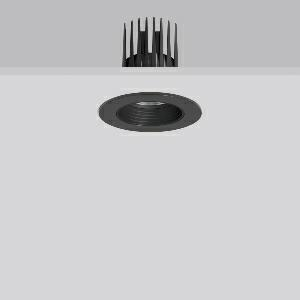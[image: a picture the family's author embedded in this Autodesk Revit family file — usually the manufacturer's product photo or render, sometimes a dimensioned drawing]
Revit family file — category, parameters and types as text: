
# Revit family: heledon_mini_e_901743_003_32de
name_source: partatom
category: Lighting Fixtures
units: mm (PartAtom-declared; Revit-internal decimal feet)

## family parameters
Cut with Voids When Loaded = No
Host = Face
Light Source = No
Part Type = Normal
Room Calculation Point = No
Round Connector Dimension = Use Diameter
Shared = No

## types (1)
- HELEDON mini E (1 x LED Modul 930, 2250 lm, 3000)
    Apparent Load = 20 VA
    Approval mark = CE
    CIE Flux Codes = 99 100 100 100 100
    Color Rendering = 90
    Color Temperature = 3000
    Default Elevation = 1800 mm
    Description = Series: HELEDON mini
Round recessed downlight. Housing: die-cast aluminium, powder-coated. Black plastic ring and recessed LED to prevent glare from the side. Optical assembly with lens made of plastic (polycarbonate) for the best homogeneous light distribution - can be changed without tools. Best colour rendering index Ra>90. Suitable for Recessed ceiling mounting. Installation without tools thanks to spring fastening system. Including separate LED converter with connecting cable 600 mm.High quality converter without flickering and stroboscopic effect. Through-wiring box (5 pole) available as accessory. The following accessories can be mounted without use of tools: interchangeable lenses, decorative glasses, honeycomb louvre, clear and frosted diffusers, white interchangeable plastic ring. 
Colour: deep black, matt (RAL 9005)
Diameter: 124 mm
Height: 3 mm
Cut-out diameter: 114 mm
Recess height: 170 mm
Luminaire: recess height: 120 mm
Lamp: LED
Socket: without socket
Colour temperature: 3000K
Colour rendering index (CRI): 92
System power: 20 W
Rated luminous flux: 2250 lm
Luminous efficiency: 113 lm/W
Control gear: Regulated power supply
Protection class: II
Type of protection: IP 20
    Height = 0 mm  [stored 0 ft]
    Lamp = 1 x LED Modul 930
    Lamp Light Flux = 2250 lm
    Lamp count = 1
    Length = 124 mm  [stored 0.406824 ft]
    Lifetime = 50000 h
    Luminous efficacy = 113 lm/W
    Manufacturer = RZB
    ModVariant = No
    Model = 901743.003
    Mounting Place = Ceiling
    Mounting Type = Recessed
    Number of Poles = 1
    OnlyDefault = Yes
    Power Factor = 1
    Product Name = HELEDON mini E
    Product group = Recessed downlights
    ProductGroupID = 402
    Protection Class = Protection class II
    Protection Degree = IP 20
    RLX_Detail_Level = 1
    RLX_Emergency_Light_Flux = 0 lm
    RLX_Emergency_Type = 0
    RLX_Emergency_Type_DB = No
    RlxData = <blob elided: 122801 chars, md5=823b8166>
    Socket = socket
    Standby Power = 0 W
    System Light Flux = 2250 lm
    System Power = 20 W
    Type Comments = Product without accessories
    Type Image = 901656.003.jpg
    URL = http://relux.com
    VarID = ---
    Voltage = 230 V
    Voltage Range = 220-240 V
    Weight = 0.00 kg
    Width = 0 mm  [stored 0 ft]

note: [stored X ft] marks values corroborated as IEEE doubles in the binary element streams (Revit-internal decimal feet)

## geometry (parser evidence)
native form markers: Blend x4, Sweep x11
no freeform markers — native parametric forms only
